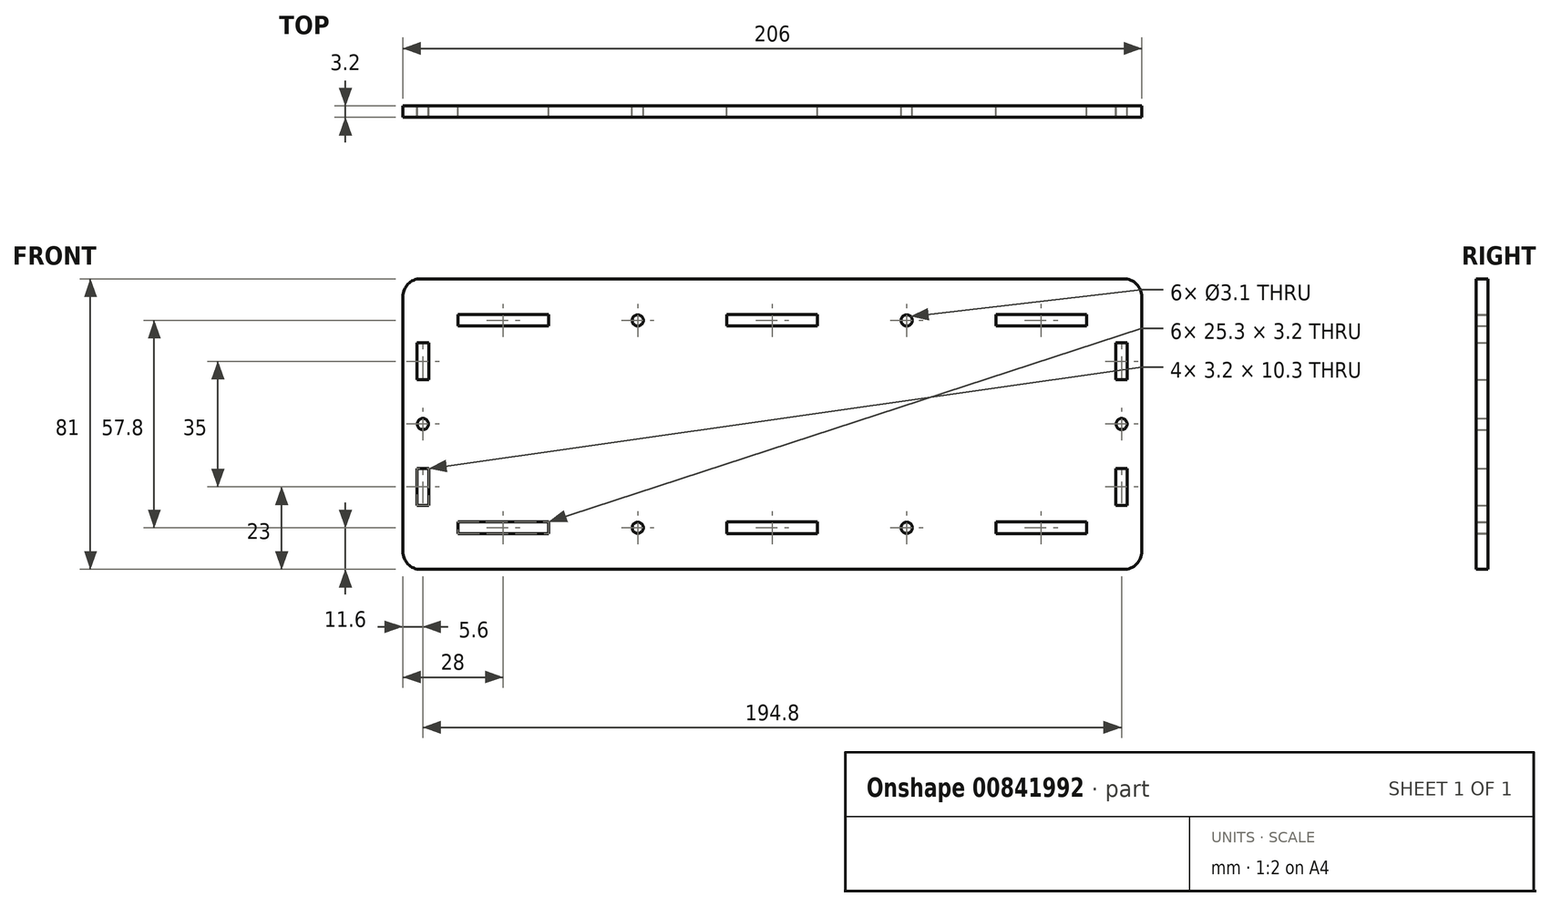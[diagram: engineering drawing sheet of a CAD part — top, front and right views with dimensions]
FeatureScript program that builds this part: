
annotation { "Feature Type Name" : "Feature", "Feature Type Description" : "" }
export const myFeature = defineFeature(function(context is Context, id is Id, definition is map)
    precondition{}
    {
        {
            assignVariable(context, id + "F0", {"name" : "mat_t", "anyValue" : 3.2});
        }
        {
            var Q0;
            Q0=qCreatedBy(makeId("Front.planeOp"),FACE);
            var sketch = newSketch(context, id + "F1", { "sketchPlane" : qUnion([Q0])});
            skLineSegment(sketch, "E0.left", {"start": v(-103, 81) * mm, "end": v(-103, 0) * mm});
            skLineSegment(sketch, "E0.right", {"start": v(103, 81) * mm, "end": v(103, 0) * mm});
            skLineSegment(sketch, "E1", {"start": v(0, 81) * mm, "end": v(0, 0) * mm, "construction": true});
            skLineSegment(sketch, "E2", {"start": v(-99, 81) * mm, "end": v(-99, 0) * mm, "construction": true});
            skLineSegment(sketch, "E3", {"start": v(99, 81) * mm, "end": v(99, 0) * mm, "construction": true});
            skLineSegment(sketch, "E4", {"start": v(-99, 0) * mm, "end": v(99, 0) * mm});
            skLineSegment(sketch, "E5", {"start": v(99, 0) * mm, "end": v(103, 0) * mm});
            skLineSegment(sketch, "E6", {"start": v(-99, 0) * mm, "end": v(-103, 0) * mm});
            skLineSegment(sketch, "E7", {"start": v(-99, 81) * mm, "end": v(99, 81) * mm});
            skLineSegment(sketch, "E8", {"start": v(99, 81) * mm, "end": v(103, 81) * mm});
            skLineSegment(sketch, "E9", {"start": v(-103, 81) * mm, "end": v(-99, 81) * mm});
            skLineSegment(sketch, "E10.bottom", {"start": v(-99, 63.15) * mm, "end": v(-95.8, 63.15) * mm});
            skLineSegment(sketch, "E10.top", {"start": v(-99, 52.85) * mm, "end": v(-95.8, 52.85) * mm});
            skLineSegment(sketch, "E10.left", {"start": v(-99, 63.15) * mm, "end": v(-99, 52.85) * mm});
            skLineSegment(sketch, "E10.right", {"start": v(-95.8, 63.15) * mm, "end": v(-95.8, 52.85) * mm});
            skLineSegment(sketch, "E11", {"start": v(-103, 40.5) * mm, "end": v(103, 40.5) * mm, "construction": true});
            skCircle(sketch, "E12", {"center": v(-97.4, 40.5) * mm, "radius": 1.55 * mm});
            skLineSegment(sketch, "E13", {"start": v(-97.4, 52.85) * mm, "end": v(-97.4, 40.5) * mm, "construction": true});
            skLineSegment(sketch, "E14.MirrorCS", {"start": v(-99, 17.85) * mm, "end": v(-95.8, 17.85) * mm});
            skLineSegment(sketch, "E15.MirrorCS", {"start": v(-99, 17.85) * mm, "end": v(-99, 28.15) * mm});
            skLineSegment(sketch, "E16.MirrorCS", {"start": v(-95.8, 17.85) * mm, "end": v(-95.8, 28.15) * mm});
            skLineSegment(sketch, "E17.MirrorCS", {"start": v(-99, 28.15) * mm, "end": v(-95.8, 28.15) * mm});
            skLineSegment(sketch, "E18.MirrorCS", {"start": v(99, 52.85) * mm, "end": v(95.8, 52.85) * mm});
            skLineSegment(sketch, "E19.MirrorCS", {"start": v(99, 63.15) * mm, "end": v(95.8, 63.15) * mm});
            skCircle(sketch, "E20.MirrorC", {"center": v(97.4, 40.5) * mm, "radius": 1.55 * mm});
            skLineSegment(sketch, "E21.MirrorCS", {"start": v(99, 17.85) * mm, "end": v(95.8, 17.85) * mm});
            skLineSegment(sketch, "E22.MirrorCS", {"start": v(99, 63.15) * mm, "end": v(99, 52.85) * mm});
            skLineSegment(sketch, "E23.MirrorCS", {"start": v(95.8, 63.15) * mm, "end": v(95.8, 52.85) * mm});
            skLineSegment(sketch, "E24.MirrorCS", {"start": v(99, 17.85) * mm, "end": v(99, 28.15) * mm});
            skLineSegment(sketch, "E25.MirrorCS", {"start": v(99, 28.15) * mm, "end": v(95.8, 28.15) * mm});
            skLineSegment(sketch, "E26.MirrorCS", {"start": v(97.4, 52.85) * mm, "end": v(97.4, 40.5) * mm, "construction": true});
            skLineSegment(sketch, "E27.MirrorCS", {"start": v(95.8, 17.85) * mm, "end": v(95.8, 28.15) * mm});
            skLineSegment(sketch, "E28", {"start": v(-103, 71) * mm, "end": v(103, 71) * mm, "construction": true});
            skLineSegment(sketch, "E29.MirrorCS", {"start": v(-103, 10) * mm, "end": v(103, 10) * mm, "construction": true});
            skLineSegment(sketch, "E30.bottom", {"start": v(-12.65, 10) * mm, "end": v(12.65, 10) * mm});
            skLineSegment(sketch, "E30.top", {"start": v(-12.65, 13.2) * mm, "end": v(12.65, 13.2) * mm});
            skLineSegment(sketch, "E30.left", {"start": v(-12.65, 10) * mm, "end": v(-12.65, 13.2) * mm});
            skLineSegment(sketch, "E30.right", {"start": v(12.65, 10) * mm, "end": v(12.65, 13.2) * mm});
            skLineSegment(sketch, "E31.bottom", {"start": v(-87.65, 10) * mm, "end": v(-62.35, 10) * mm});
            skLineSegment(sketch, "E31.top", {"start": v(-87.65, 13.2) * mm, "end": v(-62.35, 13.2) * mm});
            skLineSegment(sketch, "E31.left", {"start": v(-87.65, 10) * mm, "end": v(-87.65, 13.2) * mm});
            skLineSegment(sketch, "E31.right", {"start": v(-62.35, 10) * mm, "end": v(-62.35, 13.2) * mm});
            skLineSegment(sketch, "E32.MirrorCS", {"start": v(87.65, 10) * mm, "end": v(62.35, 10) * mm});
            skLineSegment(sketch, "E33.MirrorCS", {"start": v(62.35, 10) * mm, "end": v(62.35, 13.2) * mm});
            skLineSegment(sketch, "E34.MirrorCS", {"start": v(87.65, 10) * mm, "end": v(87.65, 13.2) * mm});
            skLineSegment(sketch, "E35.MirrorCS", {"start": v(87.65, 13.2) * mm, "end": v(62.35, 13.2) * mm});
            skLineSegment(sketch, "E36", {"start": v(-75, 13.2) * mm, "end": v(-75, 10) * mm, "construction": true});
            skLineSegment(sketch, "E37", {"start": v(75, 13.2) * mm, "end": v(75, 10) * mm, "construction": true});
            skLineSegment(sketch, "E38", {"start": v(-62.35, 11.6) * mm, "end": v(-12.65, 11.6) * mm, "construction": true});
            skCircle(sketch, "E39", {"center": v(-37.5, 11.6) * mm, "radius": 1.55 * mm});
            skCircle(sketch, "E40.MirrorC", {"center": v(37.5, 11.6) * mm, "radius": 1.55 * mm});
            skLineSegment(sketch, "E41", {"start": v(0, 13.2) * mm, "end": v(0, 10) * mm, "construction": true});
            skLineSegment(sketch, "E42.MirrorCS", {"start": v(-12.65, 71) * mm, "end": v(-12.65, 67.8) * mm});
            skLineSegment(sketch, "E43.MirrorCS", {"start": v(-62.35, 71) * mm, "end": v(-62.35, 67.8) * mm});
            skLineSegment(sketch, "E44.MirrorCS", {"start": v(12.65, 71) * mm, "end": v(12.65, 67.8) * mm});
            skLineSegment(sketch, "E45.MirrorCS", {"start": v(-62.35, 69.4) * mm, "end": v(-12.65, 69.4) * mm, "construction": true});
            skCircle(sketch, "E46.MirrorC", {"center": v(37.5, 69.4) * mm, "radius": 1.55 * mm});
            skLineSegment(sketch, "E47.MirrorCS", {"start": v(0, 67.8) * mm, "end": v(0, 71) * mm, "construction": true});
            skLineSegment(sketch, "E48.MirrorCS", {"start": v(-12.65, 67.8) * mm, "end": v(12.65, 67.8) * mm});
            skLineSegment(sketch, "E49.MirrorCS", {"start": v(87.65, 67.8) * mm, "end": v(62.35, 67.8) * mm});
            skLineSegment(sketch, "E50.MirrorCS", {"start": v(-87.65, 71) * mm, "end": v(-87.65, 67.8) * mm});
            skLineSegment(sketch, "E51.MirrorCS", {"start": v(75, 67.8) * mm, "end": v(75, 71) * mm, "construction": true});
            skLineSegment(sketch, "E52.MirrorCS", {"start": v(-87.65, 67.8) * mm, "end": v(-62.35, 67.8) * mm});
            skLineSegment(sketch, "E53.MirrorCS", {"start": v(62.35, 71) * mm, "end": v(62.35, 67.8) * mm});
            skLineSegment(sketch, "E54.MirrorCS", {"start": v(-75, 67.8) * mm, "end": v(-75, 71) * mm, "construction": true});
            skCircle(sketch, "E55.MirrorC", {"center": v(-37.5, 69.4) * mm, "radius": 1.55 * mm});
            skLineSegment(sketch, "E56.MirrorCS", {"start": v(87.65, 71) * mm, "end": v(87.65, 67.8) * mm});
            skLineSegment(sketch, "E57.MirrorCS", {"start": v(-87.65, 71) * mm, "end": v(-62.35, 71) * mm});
            skLineSegment(sketch, "E58.MirrorCS", {"start": v(87.65, 71) * mm, "end": v(62.35, 71) * mm});
            skLineSegment(sketch, "E59.MirrorCS", {"start": v(-12.65, 71) * mm, "end": v(12.65, 71) * mm});
            skLineSegment(sketch, "E60", {"start": v(-99, 23) * mm, "end": v(-95.8, 23) * mm, "construction": true});
            skLineSegment(sketch, "E61", {"start": v(-99, 58) * mm, "end": v(-95.8, 58) * mm, "construction": true});
            skSolve(sketch);
        }
        {
            var Q0;
            Q0=qSketchRegion(id+"F1",true);
            extrude(context, id + "F2", {"entities" : qUnion([Q0]), "depth" : (getVariable(context, 'mat_t')) * mm, "offsetDistance" : 25 * mm});
        }
        {
            var Q0;
            Q0=makeQuery(id+"F2.opExtrude","SWEPT_EDGE",EDGE,{"disambiguationData":[OSD([sQuery(id+"F1.wireOp",EDGE,"E0.left"),sQuery(id+"F1.wireOp",EDGE,"E9")])]});
            var Q1;
            Q1=makeQuery(id+"F2.opExtrude","SWEPT_EDGE",EDGE,{"disambiguationData":[OSD([sQuery(id+"F1.wireOp",EDGE,"E0.left"),sQuery(id+"F1.wireOp",EDGE,"E6")])]});
            var Q2;
            Q2=makeQuery(id+"F2.opExtrude","SWEPT_EDGE",EDGE,{"disambiguationData":[OSD([sQuery(id+"F1.wireOp",EDGE,"E0.right"),sQuery(id+"F1.wireOp",EDGE,"E8")])]});
            var Q3;
            Q3=makeQuery(id+"F2.opExtrude","SWEPT_EDGE",EDGE,{"disambiguationData":[OSD([sQuery(id+"F1.wireOp",EDGE,"E0.right"),sQuery(id+"F1.wireOp",EDGE,"E5")])]});
            fillet(context, id + "F3", {"entities" : qUnion([Q0, Q1, Q2, Q3]), "radius" : 5 * mm, "tangentPropagation" : true, "allowEdgeOverflow" : false});
        }
    });
